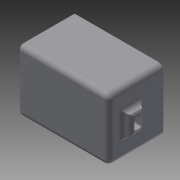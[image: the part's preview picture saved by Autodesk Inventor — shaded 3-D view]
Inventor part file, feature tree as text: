
AUTODESK INVENTOR PART (.ipt)
format: ipt  version: 2014 (Build 180170000, 170)  size: 233,472 bytes
history: native  units: mm
features: extrude x7, sketch x7, fillet x4
ambient origin geometry x8: Origin, YZ Plane, XZ Plane, XY Plane, X Axis, Y Axis, Z Axis, Center Point
bodies: Solid1 (feature_tree)
feature tree (18):
  extrude  "Extrusion1"  Depth=36.0mm
  extrude  "Extrusion2"  Depth=1.6mm
  extrude  "Extrusion3"  Depth=8.0mm
  extrude  "Extrusion4"  Depth=2.6mm
  extrude  "Extrusion5"  Depth=1.8mm
  fillet  "Fillet1"  Radius=23.0mm
  fillet  "Fillet2"  Radius=1.8mm
  extrude  "Extrusion6"  Depth=30.0mm TaperAngle=0.0deg
  extrude  "Extrusion7"  Depth=3.0mm TaperAngle=0.0deg
  fillet  "Fillet3"  Radius=8.0mm
  fillet  "Fillet4"  Radius=4.0mm
  sketch  "Sketch1"  dims[d0=53.0mm d1=36.0mm]
  sketch  "Sketch2"  dims[d2=1.6mm d3=0.0mm d4=37.0mm]
  sketch  "Sketch3"  dims[d5=8.0mm d6=8.0mm]
  sketch  "Sketch4"  dims[d7=2.6mm d8=2.6mm]
  sketch  "Sketch5"  dims[d9=7.0mm d10=7.0mm d11=23.0mm d12=0.0mm d13=1.8mm]
  sketch  "Sketch6"  dims[d14=1.8mm d15=30.0mm d16=0.0mm]
  sketch  "Sketch7"  dims[d17=3.8mm d18=3.0mm d19=0.0mm d20=8.0mm d21=4.0mm d22=0.0mm d23=3.0mm d24=3.0mm d25=6.0mm d26=4.0mm d27=4.0mm d28=0.0mm d29=4.0mm d30=0.0mm d31=3.0mm d32=3.0mm]
